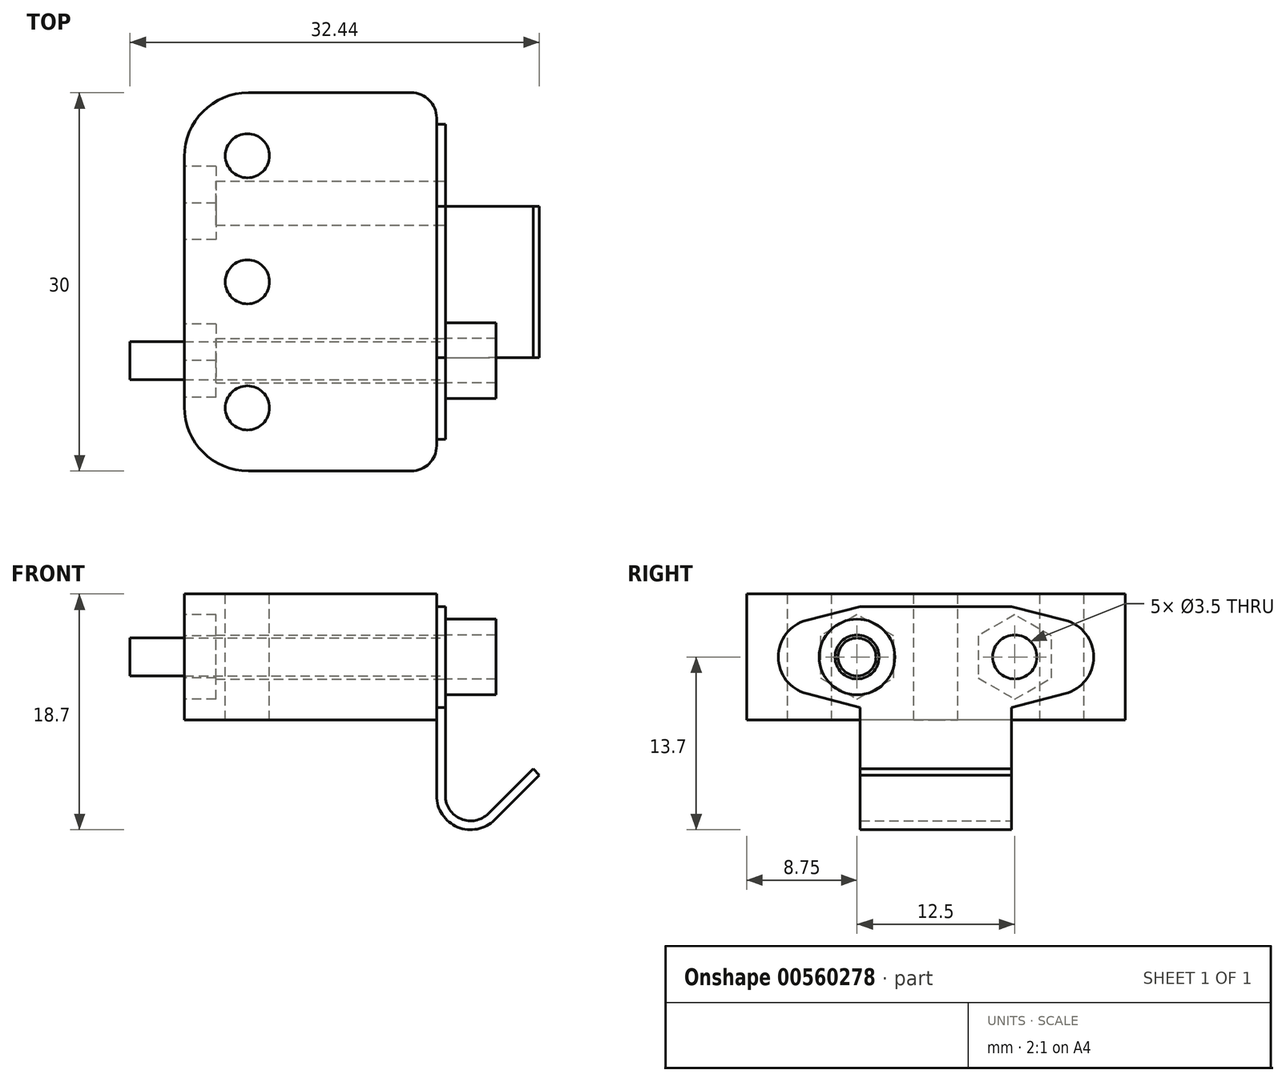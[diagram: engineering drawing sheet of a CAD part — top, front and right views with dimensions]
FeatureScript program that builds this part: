
annotation { "Feature Type Name" : "Feature", "Feature Type Description" : "" }
export const myFeature = defineFeature(function(context is Context, id is Id, definition is map)
    precondition{}
    {
        {
            var Q0;
            Q0=qCreatedBy(makeId("Front.planeOp"),FACE);
            var sketch = newSketch(context, id + "F0", { "sketchPlane" : qUnion([Q0])});
            skLineSegment(sketch, "E0", {"start": v(0.7, 15) * mm, "end": v(0, 15) * mm});
            skLineSegment(sketch, "E1", {"start": v(0, 15) * mm, "end": v(0, 0) * mm});
            skArc(sketch, "E2", {"start": v(0, 0) * mm, "mid": v(1.67, -2.5) * mm, "end": v(4.6, -1.9) * mm});
            skLineSegment(sketch, "E3", {"start": v(4.6, -1.9) * mm, "end": v(8.14, 1.63) * mm});
            skLineSegment(sketch, "E4", {"start": v(8.14, 1.63) * mm, "end": v(7.65, 2.12) * mm});
            skLineSegment(sketch, "E5", {"start": v(7.65, 2.12) * mm, "end": v(4.11, -1.41) * mm});
            skArc(sketch, "E6", {"start": v(0.7, 0) * mm, "mid": v(1.93, -1.85) * mm, "end": v(4.11, -1.41) * mm});
            skLineSegment(sketch, "E7", {"start": v(0.7, 0) * mm, "end": v(0.7, 15) * mm});
            skSolve(sketch);
        }
        {
            var Q0;
            Q0=makeQuery(id+"F0.imprint","IMPRINT",FACE,{"disambiguationData":[TD([[makeQuery(id+"F0.imprint","IMPRINT",EDGE,{"derivedFrom":sQuery(id+"F0.wireOp",EDGE,"E0")}),1.0]])]});
            extrude(context, id + "F1", {"entities" : qUnion([Q0]), "endBound" : BoundingType.SYMMETRIC, "depth" : 25 * mm, "offsetDistance" : 25.4 * mm});
        }
        {
            var Q0;
            Q0=qCreatedBy(makeId("Right.planeOp"),FACE);
            var sketch = newSketch(context, id + "F2", { "sketchPlane" : qUnion([Q0])});
            skArc(sketch, "E8", {"start": v(-10.25, 13.9) * mm, "mid": v(-12.5, 11) * mm, "end": v(-10.25, 8.1) * mm});
            skArc(sketch, "E9", {"start": v(10.25, 8.1) * mm, "mid": v(12.5, 11) * mm, "end": v(10.25, 13.9) * mm});
            skLineSegment(sketch, "E10", {"start": v(-10.25, 13.9) * mm, "end": v(-6, 15) * mm});
            skLineSegment(sketch, "E11", {"start": v(10.25, 13.9) * mm, "end": v(6, 15) * mm});
            skLineSegment(sketch, "E12", {"start": v(-10.25, 8.1) * mm, "end": v(-6, 7) * mm});
            skLineSegment(sketch, "E13", {"start": v(-6, 7) * mm, "end": v(-6, -10) * mm});
            skLineSegment(sketch, "E14", {"start": v(-6, -10) * mm, "end": v(-17.5, -10) * mm});
            skLineSegment(sketch, "E15", {"start": v(-17.5, -10) * mm, "end": v(-17.5, 20) * mm});
            skLineSegment(sketch, "E16", {"start": v(-17.5, 20) * mm, "end": v(17.5, 20) * mm});
            skLineSegment(sketch, "E17", {"start": v(17.5, 20) * mm, "end": v(17.5, -10) * mm});
            skLineSegment(sketch, "E18", {"start": v(17.5, -10) * mm, "end": v(6, -10) * mm});
            skLineSegment(sketch, "E19", {"start": v(6, -10) * mm, "end": v(6, 7) * mm});
            skLineSegment(sketch, "E20", {"start": v(6, 7) * mm, "end": v(10.25, 8.1) * mm});
            skLineSegment(sketch, "E21", {"start": v(-6, 15) * mm, "end": v(6, 15) * mm});
            skLineSegment(sketch, "E22", {"start": v(0, 20) * mm, "end": v(0, 15) * mm, "construction": true});
            skLineSegment(sketch, "E23", {"start": v(-6, 7) * mm, "end": v(6, 7) * mm, "construction": true});
            skLineSegment(sketch, "E24", {"start": v(0, 15) * mm, "end": v(0, 7) * mm, "construction": true});
            skLineSegment(sketch, "E25", {"start": v(-9.5, 11) * mm, "end": v(9.5, 11) * mm, "construction": true});
            skSolve(sketch);
        }
        {
            var Q0;
            Q0=makeQuery(id+"F2.imprint","IMPRINT",FACE,{"disambiguationData":[TD([[makeQuery(id+"F2.imprint","IMPRINT",EDGE,{"derivedFrom":sQuery(id+"F2.wireOp",EDGE,"E8")}),-1.0]])]});
            extrude(context, id + "F3", {"entities" : qUnion([Q0]), "operationType" : NewBodyOperationType.REMOVE, "endBound" : BoundingType.SYMMETRIC, "oppositeDirection" : true, "depth" : 100 * mm, "offsetDistance" : 25.4 * mm});
        }
        {
            var Q0;
            Q0=makeQuery(id+"F1.opExtrude","SWEPT_FACE",FACE,{"disambiguationData":[OSD([sQuery(id+"F0.wireOp",EDGE,"E7")])]});
            var sketch = newSketch(context, id + "F4", { "sketchPlane" : qUnion([Q0])});
            skCircle(sketch, "E26", {"center": v(-6.25, 11) * mm, "radius": 1.75 * mm});
            skCircle(sketch, "E27", {"center": v(6.25, 11) * mm, "radius": 1.75 * mm});
            skLineSegment(sketch, "E28", {"start": v(-6.25, 11) * mm, "end": v(6.25, 11) * mm, "construction": true});
            skLineSegment(sketch, "E29", {"start": v(0, 15) * mm, "end": v(0, 11) * mm, "construction": true});
            skSolve(sketch);
        }
        {
            var Q0;
            Q0=makeQuery(id+"F4.imprint","IMPRINT",FACE,{"disambiguationData":[TD([[makeQuery(id+"F4.imprint","IMPRINT",EDGE,{"derivedFrom":sQuery(id+"F4.wireOp",EDGE,"E26")}),1.0]])]});
            var Q1;
            Q1=makeQuery(id+"F4.imprint","IMPRINT",FACE,{"disambiguationData":[TD([[makeQuery(id+"F4.imprint","IMPRINT",EDGE,{"derivedFrom":sQuery(id+"F4.wireOp",EDGE,"E27")}),1.0]])]});
            extrude(context, id + "F5", {"entities" : qUnion([Q0, Q1]), "operationType" : NewBodyOperationType.REMOVE, "endBound" : BoundingType.THROUGH_ALL, "oppositeDirection" : true, "depth" : 25.4 * mm, "offsetDistance" : 25.4 * mm});
        }
        {
            var Q0;
            Q0=makeQuery(id+"F1.opExtrude","SWEPT_FACE",FACE,{"disambiguationData":[OSD([sQuery(id+"F0.wireOp",EDGE,"E7")])]});
            var sketch = newSketch(context, id + "F6", { "sketchPlane" : qUnion([Q0])});
            skCircle(sketch, "E30", {"center": v(-6.25, 11) * mm, "radius": 3 * mm});
            skSolve(sketch);
        }
        {
            var Q0;
            Q0=makeQuery(id+"F6.imprint","IMPRINT",FACE,{"disambiguationData":[TD([[makeQuery(id+"F6.imprint","IMPRINT",EDGE,{"derivedFrom":sQuery(id+"F6.wireOp",EDGE,"E30")}),1.0]])]});
            var Q1;
            Q1=makeQuery(id+"F6.imprint","IMPRINT",FACE,{"disambiguationData":[TD([[makeQuery(id+"F6.imprint","IMPRINT",EDGE,{"derivedFrom":makeQuery(id+"F5.boolean.opBoolean","COPY",EDGE,{"derivedFrom":makeQuery(id+"F5.opExtrude","CAP_EDGE",EDGE,{"disambiguationData":[OSD([sQuery(id+"F4.wireOp",EDGE,"E26")])],"isStart":true})})}),1.0]])]});
            extrude(context, id + "F7", {"entities" : qUnion([Q0, Q1]), "depth" : 4 * mm, "offsetDistance" : 25.4 * mm});
        }
        {
            var Q0;
            Q0=makeQuery(id+"F7.opExtrude","CAP_FACE",FACE,{"disambiguationData":[OSD([sQuery(id+"F6.wireOp",EDGE,"E30")])],"isStart":true});
            var sketch = newSketch(context, id + "F8", { "sketchPlane" : qUnion([Q0])});
            skCircle(sketch, "E31", {"center": v(6.25, 11) * mm, "radius": 1.5 * mm});
            skSolve(sketch);
        }
        {
            var Q0;
            Q0=makeQuery(id+"F8.imprint","IMPRINT",FACE,{"disambiguationData":[TD([[makeQuery(id+"F8.imprint","IMPRINT",EDGE,{"derivedFrom":sQuery(id+"F8.wireOp",EDGE,"E31")}),1.0]])]});
            extrude(context, id + "F9", {"entities" : qUnion([Q0]), "operationType" : NewBodyOperationType.ADD, "depth" : 25 * mm, "offsetDistance" : 25.4 * mm});
        }
        {
            var Q0;
            Q0=makeQuery(id+"F1.opExtrude","SWEPT_FACE",FACE,{"disambiguationData":[OSD([sQuery(id+"F0.wireOp",EDGE,"E1")])]});
            var sketch = newSketch(context, id + "F10", { "sketchPlane" : qUnion([Q0])});
            skLineSegment(sketch, "E32.bottom", {"start": v(-15, 6) * mm, "end": v(15, 6) * mm});
            skLineSegment(sketch, "E32.top", {"start": v(-15, 16) * mm, "end": v(15, 16) * mm});
            skLineSegment(sketch, "E32.left", {"start": v(-15, 6) * mm, "end": v(-15, 16) * mm});
            skLineSegment(sketch, "E32.right", {"start": v(15, 6) * mm, "end": v(15, 16) * mm});
            skLineSegment(sketch, "E33", {"start": v(0, 15) * mm, "end": v(0, 6) * mm, "construction": true});
            skLineSegment(sketch, "E34", {"start": v(6.25, 11) * mm, "end": v(6.25, 16) * mm, "construction": true});
            skLineSegment(sketch, "E35", {"start": v(6.25, 11) * mm, "end": v(6.25, 6) * mm, "construction": true});
            skCircle(sketch, "E36.0", {"center": v(-6.25, 11) * mm, "radius": 1.75 * mm});
            skCircle(sketch, "E36.1", {"center": v(6.25, 11) * mm, "radius": 1.75 * mm});
            skSolve(sketch);
        }
        {
            var Q0;
            Q0 = qSketchRegion(id + "F10", true);
            extrude(context, id + "F11", {"entities" : qUnion([Q0]), "depth" : 20 * mm, "offsetDistance" : 25.4 * mm});
        }
        {
            var Q0;
            Q0=qCreatedBy(makeId("Top.planeOp"),FACE);
            var sketch = newSketch(context, id + "F12", { "sketchPlane" : qUnion([Q0])});
            skCircle(sketch, "E37", {"center": v(-53.4, -32.23) * mm, "radius": 16.27 * mm});
            skSolve(sketch);
        }
        {
            var Q0;
            Q0=makeQuery(id+"F12.imprint","IMPRINT",FACE,{"disambiguationData":[TD([[makeQuery(id+"F12.imprint","IMPRINT",EDGE,{"derivedFrom":sQuery(id+"F12.wireOp",EDGE,"E37")}),1.0]])]});
            extrude(context, id + "F13", {"entities" : qUnion([Q0]), "depth" : 15 * mm, "offsetDistance" : 25.4 * mm});
        }
        {
            var Q0;
            Q0=makeQuery(id+"F13.opExtrude","SWEPT_BODY",BODY,{"disambiguationData":[OSD([sQuery(id+"F12.wireOp",EDGE,"E37")])]});
            deleteBodies(context, id + "F14", {"entities" : qUnion([Q0])});
        }
        {
            var Q0;
            Q0=makeQuery(id+"F11.opExtrude","CAP_FACE",FACE,{"disambiguationData":[OSD([sQuery(id+"F10.wireOp",EDGE,"E32.bottom"),sQuery(id+"F10.wireOp",EDGE,"E32.top"),sQuery(id+"F10.wireOp",EDGE,"E32.left"),sQuery(id+"F10.wireOp",EDGE,"E32.right"),sQuery(id+"F10.wireOp",EDGE,"E36.0"),sQuery(id+"F10.wireOp",EDGE,"E36.1")])],"isStart":false});
            var sketch = newSketch(context, id + "F15", { "sketchPlane" : qUnion([Q0])});
            skCircle(sketch, "E38.cCircle", {"center": v(6.25, 11) * mm, "radius": 2.9 * mm, "construction": true});
            skLineSegment(sketch, "E38.0", {"start": v(3.35, 12.67) * mm, "end": v(6.25, 14.35) * mm});
            skLineSegment(sketch, "E38.1", {"start": v(6.25, 14.35) * mm, "end": v(9.15, 12.67) * mm});
            skLineSegment(sketch, "E38.2", {"start": v(9.15, 12.67) * mm, "end": v(9.15, 9.33) * mm});
            skLineSegment(sketch, "E38.3", {"start": v(9.15, 9.33) * mm, "end": v(6.25, 7.65) * mm});
            skLineSegment(sketch, "E38.4", {"start": v(6.25, 7.65) * mm, "end": v(3.35, 9.33) * mm});
            skLineSegment(sketch, "E38.5", {"start": v(3.35, 9.33) * mm, "end": v(3.35, 12.67) * mm});
            skPoint(sketch, "E38.0.midPoint", {"position": v(4.8, 13.51) * mm});
            skCircle(sketch, "E39.cCircle", {"center": v(-6.25, 11) * mm, "radius": 2.9 * mm, "construction": true});
            skLineSegment(sketch, "E39.0", {"start": v(-6.25, 14.35) * mm, "end": v(-3.35, 12.67) * mm});
            skLineSegment(sketch, "E39.1", {"start": v(-3.35, 12.67) * mm, "end": v(-3.35, 9.33) * mm});
            skLineSegment(sketch, "E39.2", {"start": v(-3.35, 9.33) * mm, "end": v(-6.25, 7.65) * mm});
            skLineSegment(sketch, "E39.3", {"start": v(-6.25, 7.65) * mm, "end": v(-9.15, 9.33) * mm});
            skLineSegment(sketch, "E39.4", {"start": v(-9.15, 9.33) * mm, "end": v(-9.15, 12.67) * mm});
            skLineSegment(sketch, "E39.5", {"start": v(-9.15, 12.67) * mm, "end": v(-6.25, 14.35) * mm});
            skPoint(sketch, "E39.0.midPoint", {"position": v(-4.8, 13.51) * mm});
            skSolve(sketch);
        }
        {
            var Q0;
            Q0=makeQuery(id+"F15.imprint","IMPRINT",FACE,{"disambiguationData":[TD([[makeQuery(id+"F15.imprint","IMPRINT",EDGE,{"derivedFrom":sQuery(id+"F15.wireOp",EDGE,"E39.0")}),-1.0]])]});
            var Q1;
            Q1=makeQuery(id+"F15.imprint","IMPRINT",FACE,{"disambiguationData":[TD([[makeQuery(id+"F15.imprint","IMPRINT",EDGE,{"derivedFrom":sQuery(id+"F15.wireOp",EDGE,"E38.0")}),-1.0]])]});
            extrude(context, id + "F16", {"entities" : qUnion([Q0, Q1]), "operationType" : NewBodyOperationType.REMOVE, "oppositeDirection" : true, "depth" : 2.5 * mm, "offsetDistance" : 25.4 * mm});
        }
        {
            var Q0;
            Q0=makeQuery(id+"F11.opExtrude","SWEPT_FACE",FACE,{"disambiguationData":[OSD([sQuery(id+"F10.wireOp",EDGE,"E32.top")])]});
            var sketch = newSketch(context, id + "F17", { "sketchPlane" : qUnion([Q0])});
            skLineSegment(sketch, "E40", {"start": v(-20, 0) * mm, "end": v(0, 0) * mm, "construction": true});
            skLineSegment(sketch, "E41", {"start": v(-15, 0) * mm, "end": v(-15, 10) * mm, "construction": true});
            skLineSegment(sketch, "E42", {"start": v(-15, 0) * mm, "end": v(-15, -10) * mm, "construction": true});
            skCircle(sketch, "E43", {"center": v(-15, 10) * mm, "radius": 1.75 * mm});
            skCircle(sketch, "E44", {"center": v(-15, -10) * mm, "radius": 1.75 * mm});
            skCircle(sketch, "E45", {"center": v(-15, 0) * mm, "radius": 1.75 * mm});
            skSolve(sketch);
        }
        {
            var Q0;
            Q0=makeQuery(id+"F17.imprint","IMPRINT",FACE,{"disambiguationData":[TD([[makeQuery(id+"F17.imprint","IMPRINT",EDGE,{"derivedFrom":sQuery(id+"F17.wireOp",EDGE,"E43")}),1.0]])]});
            var Q1;
            Q1=makeQuery(id+"F17.imprint","IMPRINT",FACE,{"disambiguationData":[TD([[makeQuery(id+"F17.imprint","IMPRINT",EDGE,{"derivedFrom":sQuery(id+"F17.wireOp",EDGE,"E45")}),1.0]])]});
            var Q2;
            Q2=makeQuery(id+"F17.imprint","IMPRINT",FACE,{"disambiguationData":[TD([[makeQuery(id+"F17.imprint","IMPRINT",EDGE,{"derivedFrom":sQuery(id+"F17.wireOp",EDGE,"E44")}),1.0]])]});
            extrude(context, id + "F18", {"entities" : qUnion([Q0, Q1, Q2]), "operationType" : NewBodyOperationType.REMOVE, "endBound" : BoundingType.THROUGH_ALL, "oppositeDirection" : true, "depth" : 25.4 * mm, "offsetDistance" : 25.4 * mm});
        }
        {
            var Q0;
            Q0=makeQuery(id+"F11.opExtrude","CAP_EDGE",EDGE,{"disambiguationData":[OSD([sQuery(id+"F10.wireOp",EDGE,"E32.left")])],"isStart":true});
            var Q1;
            Q1=makeQuery(id+"F11.opExtrude","CAP_EDGE",EDGE,{"disambiguationData":[OSD([sQuery(id+"F10.wireOp",EDGE,"E32.right")])],"isStart":true});
            fillet(context, id + "F19", {"entities" : qUnion([Q0, Q1]), "radius" : 2 * mm, "tangentPropagation" : true, "allowEdgeOverflow" : false});
        }
        {
            var Q0;
            Q0=makeQuery(id+"F11.opExtrude","CAP_EDGE",EDGE,{"disambiguationData":[OSD([sQuery(id+"F10.wireOp",EDGE,"E32.right")])],"isStart":false});
            var Q1;
            Q1=makeQuery(id+"F11.opExtrude","CAP_EDGE",EDGE,{"disambiguationData":[OSD([sQuery(id+"F10.wireOp",EDGE,"E32.left")])],"isStart":false});
            fillet(context, id + "F20", {"entities" : qUnion([Q0, Q1]), "radius" : 5.08 * mm, "tangentPropagation" : true, "allowEdgeOverflow" : false});
        }
    });
